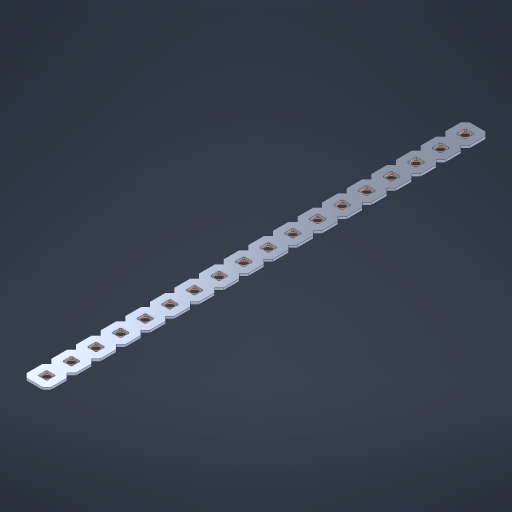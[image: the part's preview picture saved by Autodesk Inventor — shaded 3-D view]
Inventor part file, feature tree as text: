
AUTODESK INVENTOR PART (.ipt)
format: ipt  version: 2023 (Build 270158000, 158)  size: 492,032 bytes
history: native  units: in
note: dims shown in document units (in); Inventor stores cm internally (conversion verified against a paired STEP export)
features: other x19, extrude x17, sketch x2, pattern_linear x1
ambient origin geometry x8: Origin, YZ Plane, XZ Plane, XY Plane, X Axis, Y Axis, Z Axis, Center Point
bodies: Solid1 (feature_tree), Body (feature_tree)
feature tree (39):
  pattern_linear  "Rectangular Pattern1"  Spacing1=0.09in  [1 undecoded]
  sketch  "Sketch1"  dims[d1=0.5in]
  sketch  "Sketch2"  dims[d2=0.182in d3=0.09in d4=0.09in d5=0.09in d6=0.09in d7=0.09in d8=0.09in d9=0.09in d10=0.09in d11=0.02in d13=0.0in d14=0.172in d15=0.0625in d16=0.0in d19=0.5in d22=0.5in]
  other  "Srf1"
  other  "Srf126"
  other  "Srf127"
  other  "Srf128"
  other  "Srf129"
  other  "Srf130"
  other  "Srf131"
  other  "Srf250"
  other  "Srf251"
  other  "Srf252"
  other  "Srf253"
  other  "Srf254"
  other  "Srf255"
  other  "Srf256"
  other  "Srf257"
  other  "Srf258"
  other  "Srf259"
  other  "Srf260"
  other  "Circle"
  extrude  "ExtrusionSrf126"  Depth=0.09in
  extrude  "ExtrusionSrf127"  Depth=0.09in
  extrude  "ExtrusionSrf128"  Depth=0.09in
  extrude  "ExtrusionSrf129"  Depth=0.09in
  extrude  "ExtrusionSrf130"  Depth=0.09in
  extrude  "ExtrusionSrf131"  Depth=0.09in
  extrude  "ExtrusionSrf250"  Depth=0.09in
  extrude  "ExtrusionSrf251"  Depth=0.02in
  extrude  "ExtrusionSrf252"  TaperAngle=0.0deg  [1 undecoded]
  extrude  "ExtrusionSrf253"  Depth=0.5in
  extrude  "ExtrusionSrf254"  Depth=0.5in TaperAngle=0.0deg
  extrude  "ExtrusionSrf255"  Depth=0.5in
  extrude  "ExtrusionSrf256"  Depth=0.5in
  extrude  "ExtrusionSrf257"  [1 undecoded]
  extrude  "ExtrusionSrf258"  [1 undecoded]
  extrude  "ExtrusionSrf259"  [1 undecoded]
  extrude  "ExtrusionSrf260"  [1 undecoded]
note: 6 required parameter values undecoded (feature->parameter linkage not recoverable at this tier; creation-order binding heuristic only, values carry confidence <= 0.55)
